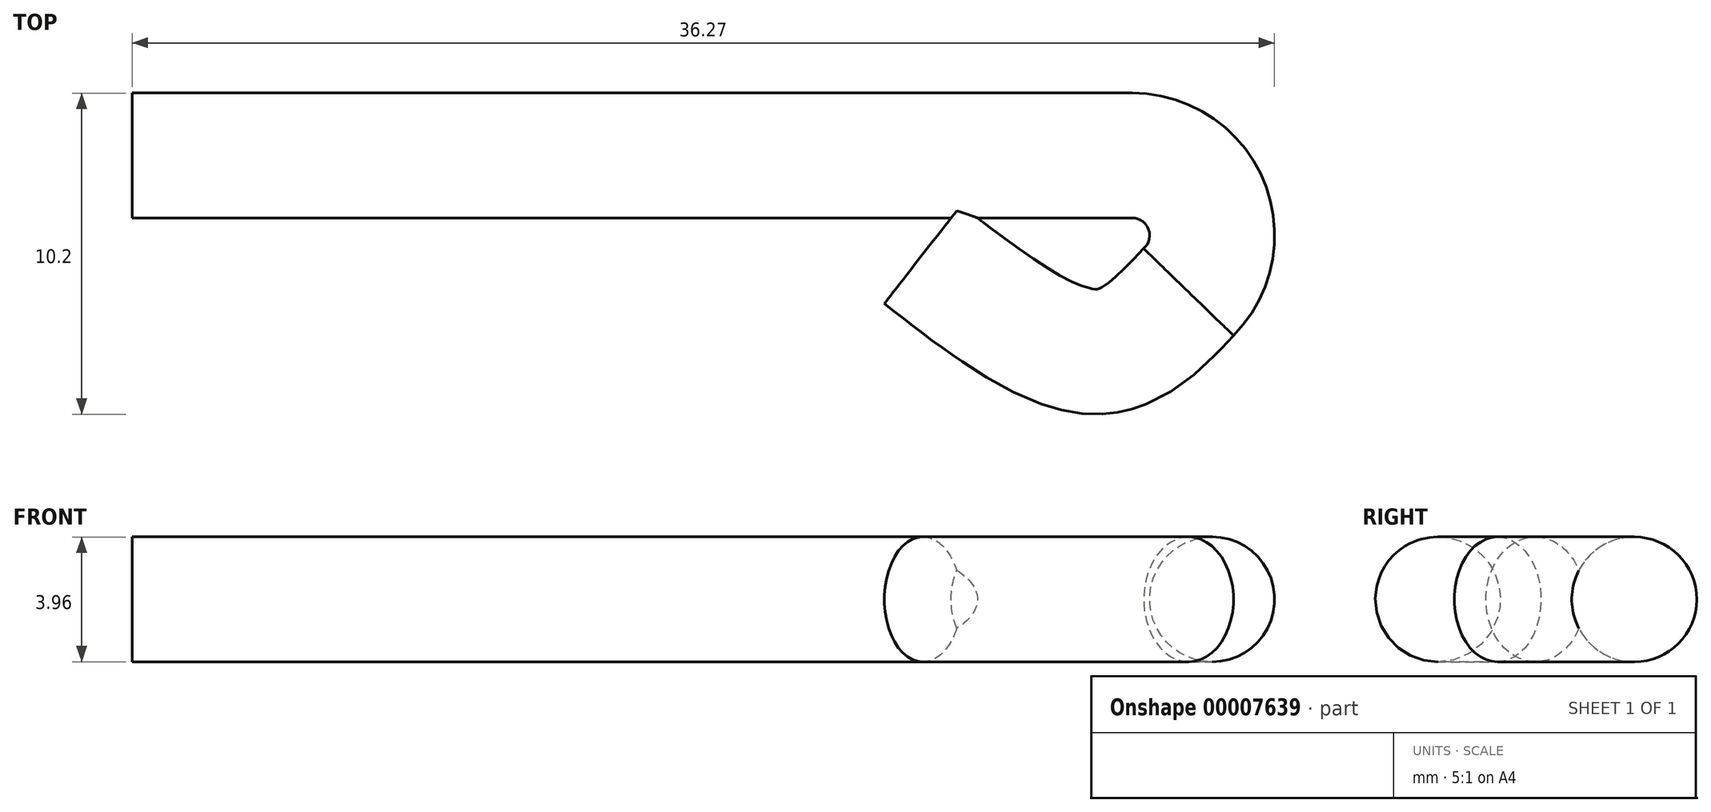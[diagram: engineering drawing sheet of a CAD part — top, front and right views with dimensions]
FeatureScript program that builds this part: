
annotation { "Feature Type Name" : "Feature", "Feature Type Description" : "" }
export const myFeature = defineFeature(function(context is Context, id is Id, definition is map)
    precondition{}
    {
        {
            var Q0;
            Q0=qCreatedBy(makeId("Top.planeOp"),FACE);
            var sketch = newSketch(context, id + "F0", { "sketchPlane" : qUnion([Q0])});
            skLineSegment(sketch, "E0", {"start": v(0, 0) * mm, "end": v(31.75, 0) * mm});
            skArc(sketch, "E1", {"start": v(31.75, 0) * mm, "mid": v(34.1, -1.57) * mm, "end": v(33.54, -4.34) * mm});
            skFitSpline(sketch, "E2", {"points": [v(33.54, -4.34) * mm, v(30.69, -6.23) * mm, v(25.1, -3.14) * mm], "startDerivative": vector(-6.13, -6.56) * mm, "endDerivative": vector(-10.52, 8.2) * mm});
            skSolve(sketch);
        }
        {
            var Q0;
            Q0=qCreatedBy(makeId("Right.planeOp"),FACE);
            var sketch = newSketch(context, id + "F1", { "sketchPlane" : qUnion([Q0])});
            skCircle(sketch, "E3", {"center": v(0, 0) * mm, "radius": 1.98 * mm});
            skSolve(sketch);
        }
        {
            var Q0;
            Q0=makeQuery(id+"F1.imprint","IMPRINT",FACE,{"disambiguationData":[TD([[makeQuery(id+"F1.imprint","IMPRINT",EDGE,{"derivedFrom":sQuery(id+"F1.wireOp",EDGE,"E3")}),1.0]])]});
            var Q1;
            Q1=sQuery(id+"F0.wireOp",EDGE,"E0");
            var Q2;
            Q2=sQuery(id+"F0.wireOp",EDGE,"E1");
            var Q3;
            Q3=sQuery(id+"F0.wireOp",EDGE,"E2");
            sweep(context, id + "F2", {"profiles" : qUnion([Q0]), "path" : qUnion([Q1, Q2, Q3])});
        }
    });
